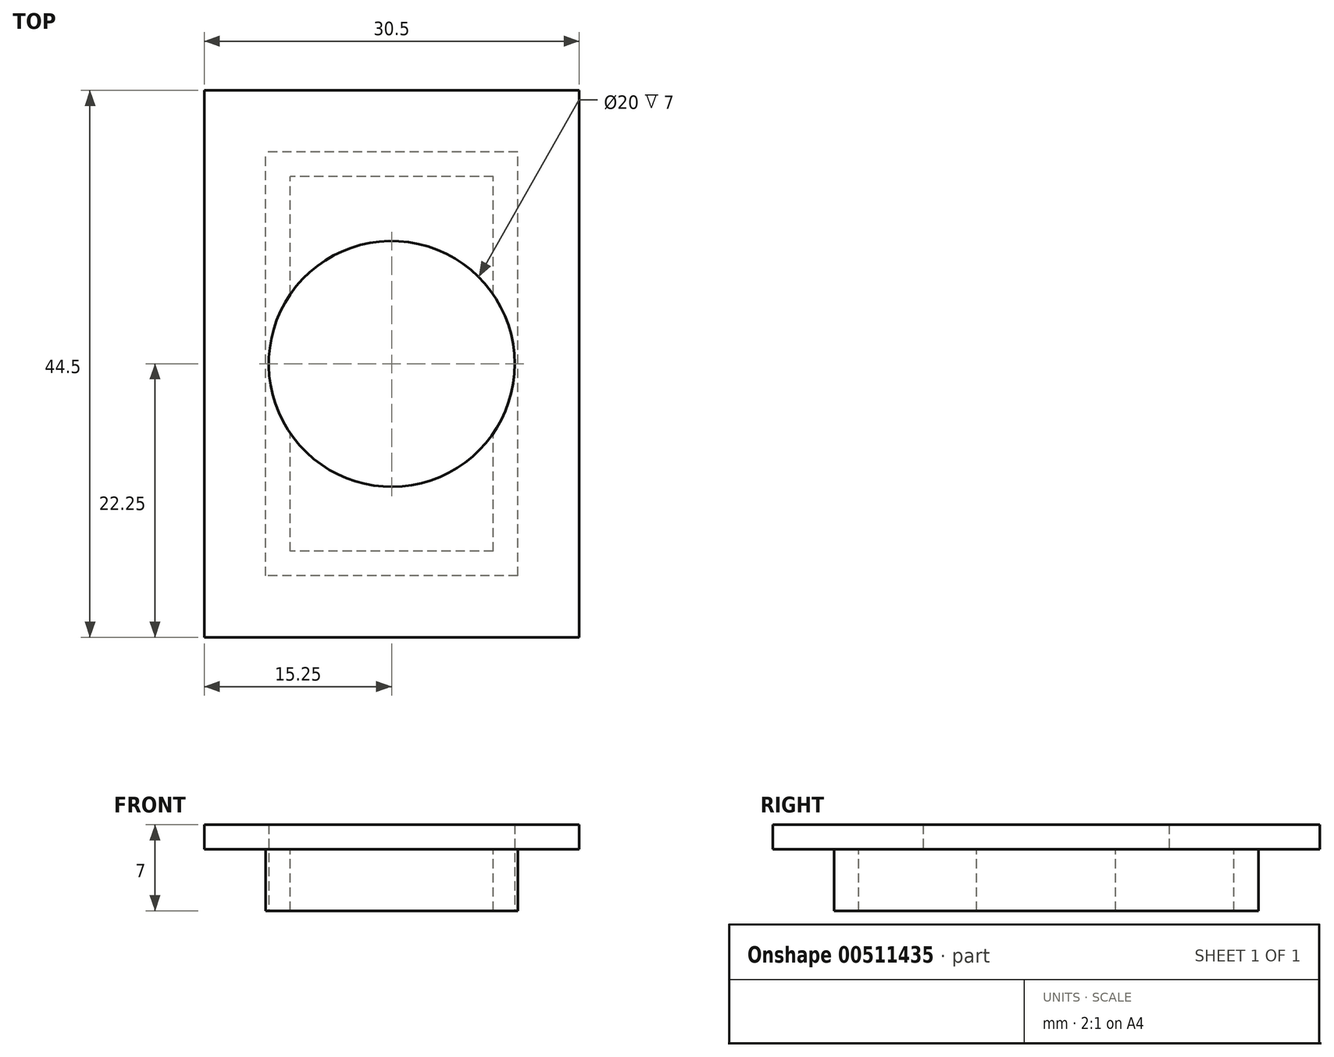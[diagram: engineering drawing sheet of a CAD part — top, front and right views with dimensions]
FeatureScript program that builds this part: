
annotation { "Feature Type Name" : "Feature", "Feature Type Description" : "" }
export const myFeature = defineFeature(function(context is Context, id is Id, definition is map)
    precondition{}
    {
        {
            var Q0;
            Q0=qCreatedBy(makeId("Top.planeOp"),FACE);
            var sketch = newSketch(context, id + "F0", { "sketchPlane" : qUnion([Q0])});
            skLineSegment(sketch, "E0.bottom", {"start": v(10.25, -17.25) * mm, "end": v(-10.25, -17.25) * mm});
            skLineSegment(sketch, "E0.top", {"start": v(10.25, 17.25) * mm, "end": v(-10.25, 17.25) * mm});
            skLineSegment(sketch, "E0.left", {"start": v(10.25, -17.25) * mm, "end": v(10.25, 17.25) * mm});
            skLineSegment(sketch, "E0.right", {"start": v(-10.25, -17.25) * mm, "end": v(-10.25, 17.25) * mm});
            skPoint(sketch, "E0.middle", {"position": v(0, 0) * mm});
            skCircle(sketch, "E1", {"center": v(0, 0) * mm, "radius": 10 * mm});
            skLineSegment(sketch, "E2.0", {"start": v(15.25, 22.25) * mm, "end": v(-15.25, 22.25) * mm});
            skLineSegment(sketch, "E2.1", {"start": v(15.25, -22.25) * mm, "end": v(15.25, 22.25) * mm});
            skLineSegment(sketch, "E2.2", {"start": v(15.25, -22.25) * mm, "end": v(-15.25, -22.25) * mm});
            skLineSegment(sketch, "E2.3", {"start": v(-15.25, -22.25) * mm, "end": v(-15.25, 22.25) * mm});
            skLineSegment(sketch, "E3.0", {"start": v(8.25, 15.25) * mm, "end": v(-8.25, 15.25) * mm});
            skLineSegment(sketch, "E3.1", {"start": v(8.25, -15.25) * mm, "end": v(8.25, 15.25) * mm});
            skLineSegment(sketch, "E3.2", {"start": v(8.25, -15.25) * mm, "end": v(-8.25, -15.25) * mm});
            skLineSegment(sketch, "E3.3", {"start": v(-8.25, -15.25) * mm, "end": v(-8.25, 15.25) * mm});
            skSolve(sketch);
        }
        {
            var Q0;
            Q0=qSketchRegion(id+"F0",true);
            var Q1;
            Q1=makeQuery(id+"F0.imprint","IMPRINT",FACE,{"disambiguationData":[TD([[makeQuery(id+"F0.imprint","IMPRINT",EDGE,{"derivedFrom":sQuery(id+"F0.wireOp",EDGE,"E0.bottom")}),-1.0]])]});
            var Q2;
            {var subQ5=sQuery(id+"F0.wireOp",EDGE,"E3.0");Q2=makeQuery(id+"F0.imprint","IMPRINT",FACE,{"disambiguationData":[TD([[makeQuery(id+"F0.imprint","IMPRINT",EDGE,{"derivedFrom":subQ5}),1.0]])]});}
            var Q3;
            {var subQ5=sQuery(id+"F0.wireOp",EDGE,"E3.2");Q3=makeQuery(id+"F0.imprint","IMPRINT",FACE,{"disambiguationData":[TD([[makeQuery(id+"F0.imprint","IMPRINT",EDGE,{"derivedFrom":subQ5}),-1.0]])]});}
            extrude(context, id + "F1", {"entities" : qUnion([Q0, Q1, Q2, Q3]), "depth" : 2 * mm, "offsetDistance" : 25 * mm});
        }
        {
            var Q0;
            Q0=makeQuery(id+"F0.imprint","IMPRINT",FACE,{"disambiguationData":[TD([[makeQuery(id+"F0.imprint","IMPRINT",EDGE,{"derivedFrom":sQuery(id+"F0.wireOp",EDGE,"E0.bottom")}),-1.0]])]});
            extrude(context, id + "F2", {"entities" : qUnion([Q0]), "operationType" : NewBodyOperationType.ADD, "oppositeDirection" : true, "depth" : 5 * mm, "offsetDistance" : 25 * mm});
        }
    });
